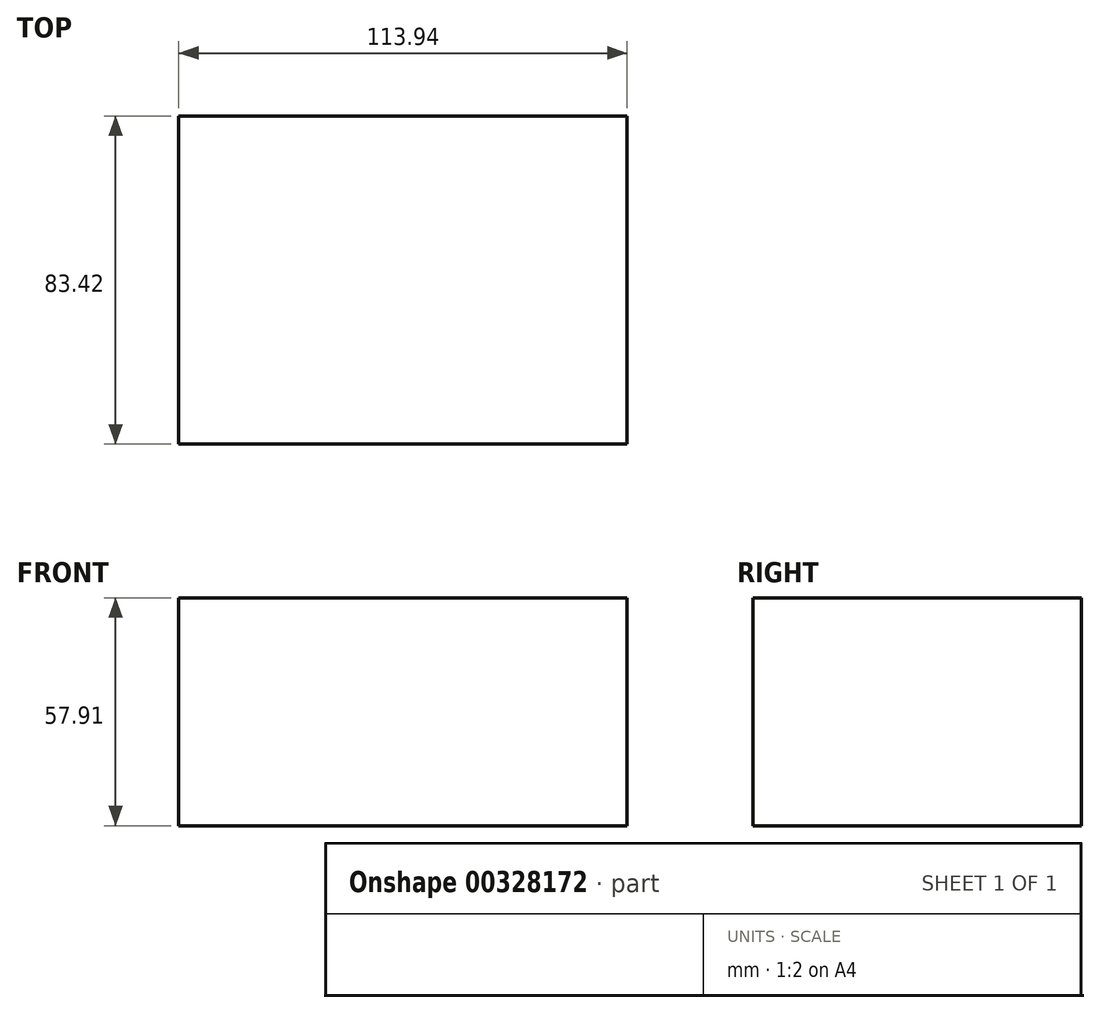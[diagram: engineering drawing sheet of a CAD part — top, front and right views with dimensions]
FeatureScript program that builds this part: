
annotation { "Feature Type Name" : "Feature", "Feature Type Description" : "" }
export const myFeature = defineFeature(function(context is Context, id is Id, definition is map)
    precondition{}
    {
        {
            var Q0;
            Q0=qCreatedBy(makeId("Top.planeOp"),FACE);
            var sketch = newSketch(context, id + "F0", { "sketchPlane" : qUnion([Q0])});
            skLineSegment(sketch, "E0.bottom", {"start": v(-56.97, -41.7) * mm, "end": v(56.97, -41.7) * mm});
            skLineSegment(sketch, "E0.top", {"start": v(-56.97, 41.7) * mm, "end": v(56.97, 41.7) * mm});
            skLineSegment(sketch, "E0.left", {"start": v(-56.97, -41.7) * mm, "end": v(-56.97, 41.7) * mm});
            skLineSegment(sketch, "E0.right", {"start": v(56.97, -41.7) * mm, "end": v(56.97, 41.7) * mm});
            skPoint(sketch, "E0.middle", {"position": v(0, 0) * mm});
            skSolve(sketch);
        }
        {
            var Q0;
            Q0 = qSketchRegion(id + "F0", true);
            extrude(context, id + "F1", {"entities" : qUnion([Q0]), "depth" : 57.9 * mm});
        }
    });
